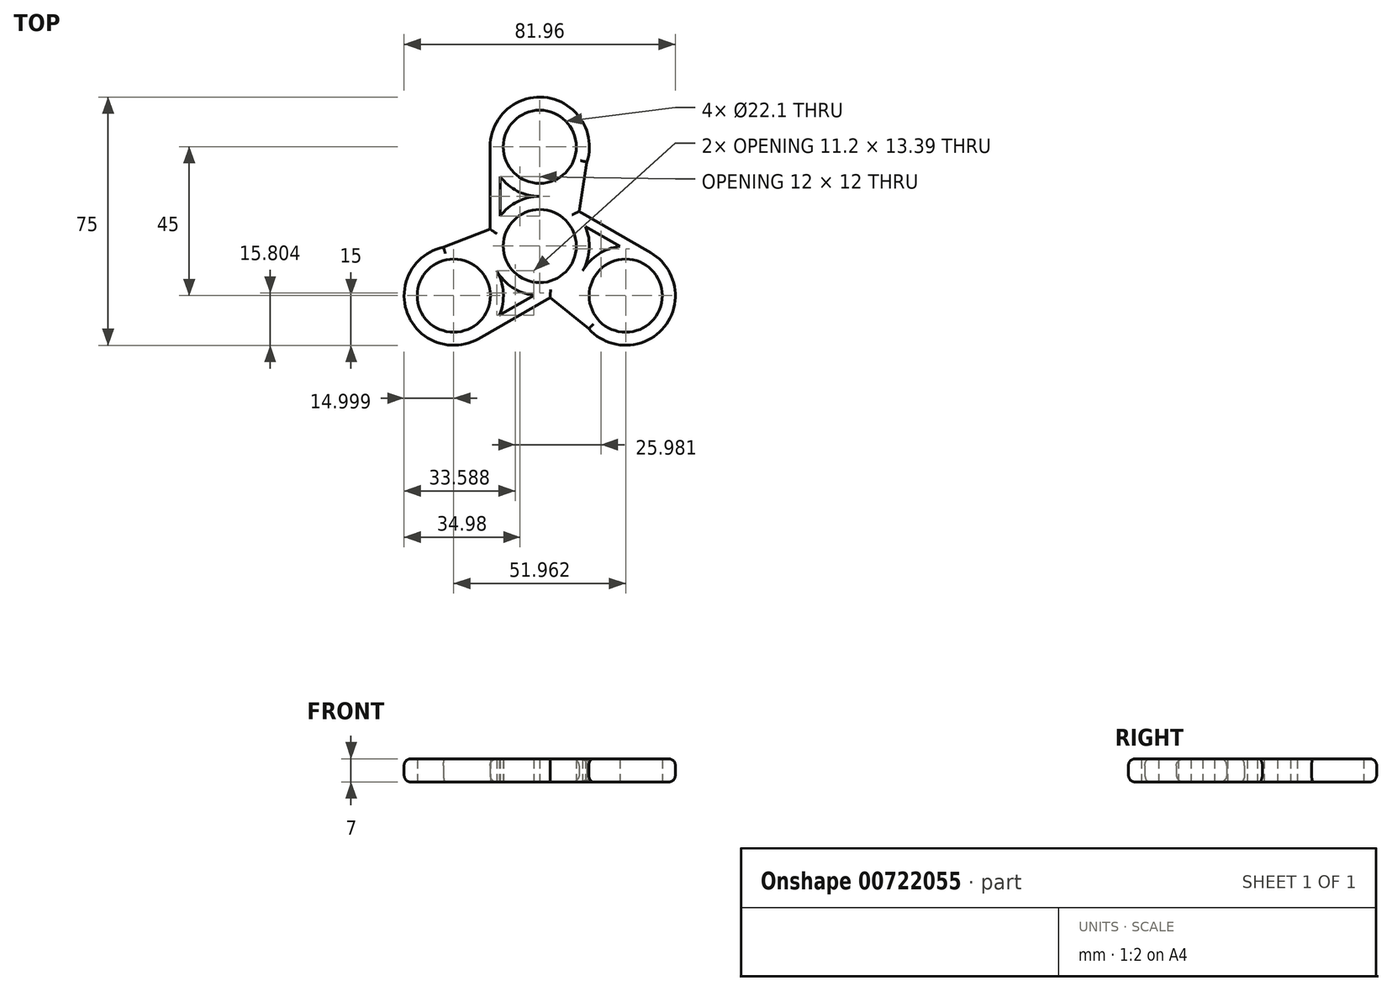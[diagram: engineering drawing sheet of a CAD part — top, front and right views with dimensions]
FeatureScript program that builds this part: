
annotation { "Feature Type Name" : "Feature", "Feature Type Description" : "" }
export const myFeature = defineFeature(function(context is Context, id is Id, definition is map)
    precondition{}
    {
        {
            var Q0;
            Q0=qCreatedBy(makeId("Top.planeOp"),FACE);
            var sketch = newSketch(context, id + "F0", { "sketchPlane" : qUnion([Q0])});
            skCircle(sketch, "E0", {"center": v(0, 0) * mm, "radius": 11.05 * mm});
            skCircle(sketch, "E1", {"center": v(0, 0) * mm, "radius": 15 * mm});
            skCircle(sketch, "E2", {"center": v(0, 30) * mm, "radius": 11.05 * mm});
            skCircle(sketch, "E3", {"center": v(0, 30) * mm, "radius": 15 * mm});
            skCircle(sketch, "E4", {"center": v(-25.98, -15) * mm, "radius": 11.05 * mm});
            skCircle(sketch, "E5", {"center": v(-25.98, -15) * mm, "radius": 15 * mm});
            skCircle(sketch, "E6", {"center": v(25.98, -15) * mm, "radius": 11.05 * mm});
            skCircle(sketch, "E7", {"center": v(25.98, -15) * mm, "radius": 15 * mm});
            skLineSegment(sketch, "E8", {"start": v(0, 30) * mm, "end": v(0, 0) * mm, "construction": true});
            skLineSegment(sketch, "E9", {"start": v(-25.98, -15) * mm, "end": v(0, 0) * mm, "construction": true});
            skLineSegment(sketch, "E10", {"start": v(25.98, -15) * mm, "end": v(0, 0) * mm, "construction": true});
            skLineSegment(sketch, "E11", {"start": v(0, 30) * mm, "end": v(-15, 30) * mm, "construction": true});
            skLineSegment(sketch, "E12", {"start": v(-15, 30) * mm, "end": v(15, 30) * mm, "construction": true});
            skLineSegment(sketch, "E13", {"start": v(-15, 30) * mm, "end": v(-15, 0) * mm});
            skLineSegment(sketch, "E14", {"start": v(-12, 21) * mm, "end": v(-12, 9) * mm});
            skLineSegment(sketch, "E15", {"start": v(25.98, -15) * mm, "end": v(33.48, -2) * mm, "construction": true});
            skLineSegment(sketch, "E16", {"start": v(33.48, -2) * mm, "end": v(18.48, -28) * mm, "construction": true});
            skLineSegment(sketch, "E17", {"start": v(33.48, -2) * mm, "end": v(7.5, 13) * mm});
            skLineSegment(sketch, "E18", {"start": v(13.8, 5.9) * mm, "end": v(24.19, -0.1) * mm});
            skLineSegment(sketch, "E19", {"start": v(-25.98, -15) * mm, "end": v(-18.48, -28) * mm, "construction": true});
            skLineSegment(sketch, "E20", {"start": v(-18.48, -28) * mm, "end": v(7.5, -13) * mm});
            skLineSegment(sketch, "E21", {"start": v(15, 30) * mm, "end": v(11.9, 10.45) * mm});
            skLineSegment(sketch, "E22", {"start": v(-12.19, -20.9) * mm, "end": v(-1.8, -14.9) * mm});
            skLineSegment(sketch, "E23", {"start": v(18.48, -28) * mm, "end": v(3.1, -15.53) * mm});
            skLineSegment(sketch, "E24", {"start": v(-25.98, -15) * mm, "end": v(-33.48, -2) * mm, "construction": true});
            skLineSegment(sketch, "E25", {"start": v(-33.48, -2) * mm, "end": v(-15, 5.08) * mm});
            skSolve(sketch);
        }
        {
            var Q0;
            Q0 = qSketchRegion(id + "F0", true);
            var Q1;
            Q1=makeQuery(id+"F0.imprint","IMPRINT",FACE,{"disambiguationData":[TD([[makeQuery(id+"F0.imprint","IMPRINT",EDGE,{"derivedFrom":sQuery(id+"F0.wireOp",EDGE,"E0")}),-1.0]])]});
            extrude(context, id + "F1", {"entities" : qUnion([Q0, Q1]), "depth" : 7 * mm, "offsetDistance" : 25 * mm});
        }
        {
            var Q0;
            Q0=makeQuery(id+"F1.opExtrude","CAP_EDGE",EDGE,{"disambiguationData":[OSD([sQuery(id+"F0.wireOp",EDGE,"E17")])],"isStart":true});
            var Q1;
            {var subQ0=sQuery(id+"F0.wireOp",EDGE,"E7");var subQ1=sQuery(id+"F0.wireOp",EDGE,"E23");var subQ2=makeQuery(id+"F0.imprint","INTERSECT",VERTEX,{"disambiguationData":[OD(0.0)],"derivedFrom":[subQ0,subQ1]});Q1=makeQuery(id+"F1.opExtrude","CAP_EDGE",EDGE,{"disambiguationData":[OSD([subQ0]),TDD([makeQuery(id+"F0.imprint","IMPRINT",EDGE,{"disambiguationData":[TD([[subQ2,1.0]])],"derivedFrom":subQ0}),makeQuery(id+"F0.imprint","IMPRINT",EDGE,{"disambiguationData":[TD([[makeQuery(id+"F0.imprint","INTERSECT",VERTEX,{"derivedFrom":[subQ0,sQuery(id+"F0.wireOp",EDGE,"E17")]}),1.0]])],"derivedFrom":subQ0})])],"isStart":true});}
            var Q2;
            Q2=makeQuery(id+"F1.opExtrude","CAP_EDGE",EDGE,{"disambiguationData":[OSD([sQuery(id+"F0.wireOp",EDGE,"E23")])],"isStart":true});
            var Q3;
            Q3=makeQuery(id+"F1.opExtrude","CAP_EDGE",EDGE,{"disambiguationData":[OSD([sQuery(id+"F0.wireOp",EDGE,"E20")])],"isStart":true});
            var Q4;
            Q4=makeQuery(id+"F1.opExtrude","CAP_EDGE",EDGE,{"disambiguationData":[OSD([sQuery(id+"F0.wireOp",EDGE,"E25")])],"isStart":true});
            var Q5;
            Q5=makeQuery(id+"F1.opExtrude","CAP_EDGE",EDGE,{"disambiguationData":[OSD([sQuery(id+"F0.wireOp",EDGE,"E13")])],"isStart":true});
            var Q6;
            Q6=makeQuery(id+"F1.opExtrude","CAP_EDGE",EDGE,{"disambiguationData":[OSD([sQuery(id+"F0.wireOp",EDGE,"E21")])],"isStart":true});
            var Q7;
            Q7=makeQuery(id+"F1.opExtrude","CAP_EDGE",EDGE,{"disambiguationData":[OSD([sQuery(id+"F0.wireOp",EDGE,"E13")])],"isStart":false});
            var Q8;
            Q8=makeQuery(id+"F1.opExtrude","CAP_EDGE",EDGE,{"disambiguationData":[OSD([sQuery(id+"F0.wireOp",EDGE,"E25")])],"isStart":false});
            var Q9;
            Q9=makeQuery(id+"F1.opExtrude","CAP_EDGE",EDGE,{"disambiguationData":[OSD([sQuery(id+"F0.wireOp",EDGE,"E20")])],"isStart":false});
            var Q10;
            Q10=makeQuery(id+"F1.opExtrude","CAP_EDGE",EDGE,{"disambiguationData":[OSD([sQuery(id+"F0.wireOp",EDGE,"E23")])],"isStart":false});
            var Q11;
            Q11=makeQuery(id+"F1.opExtrude","CAP_EDGE",EDGE,{"disambiguationData":[OSD([sQuery(id+"F0.wireOp",EDGE,"E17")])],"isStart":false});
            var Q12;
            Q12=makeQuery(id+"F1.opExtrude","CAP_EDGE",EDGE,{"disambiguationData":[OSD([sQuery(id+"F0.wireOp",EDGE,"E21")])],"isStart":false});
            fillet(context, id + "F2", {"entities" : qUnion([Q0, Q1, Q2, Q3, Q4, Q5, Q6, Q7, Q8, Q9, Q10, Q11, Q12]), "radius" : 2 * mm, "tangentPropagation" : true, "allowEdgeOverflow" : false});
        }
    });
